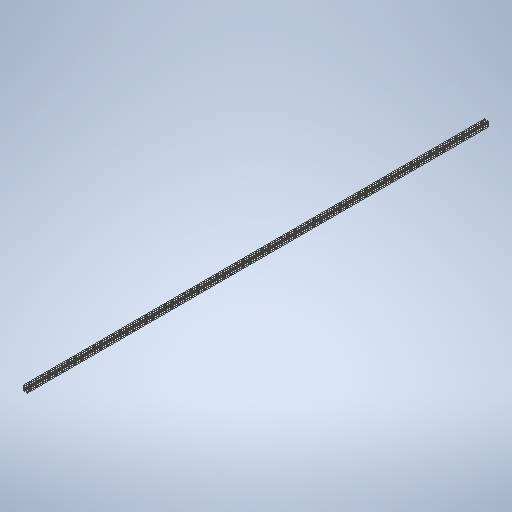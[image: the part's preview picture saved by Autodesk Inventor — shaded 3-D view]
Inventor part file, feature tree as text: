
AUTODESK INVENTOR PART (.ipt)
format: ipt  version: 2025.2 (Build 292293000, 293)  size: 358,400 bytes
history: native  units: mm
features: mirror x2, other x1, extrude x1, sketch x1
ambient origin geometry x8: Origin, YZ Plane, XZ Plane, XY Plane, X Axis, Y Axis, Z Axis, Center Point
bodies: Body1 (feature_tree)
feature tree (5):
  other  "Sólido1"
  extrude  "Extrusão1"  Depth=5.0mm
  mirror  "Espelhar1"
  mirror  "Espelhar2"
  sketch  "Esboço1"  dims[d0=20.0mm d2=5.0mm d3=6.0mm d5=2.0mm d7=1.0mm d8=6.0mm d9=1.0mm d10=0.5mm d11=0.5mm d12=0.5mm d14=0.5mm d15=0.5mm d16=10.0mm d17=2.5mm d18=2000.0mm d19=0.0mm d20=0.5mm d21=0.5mm]
